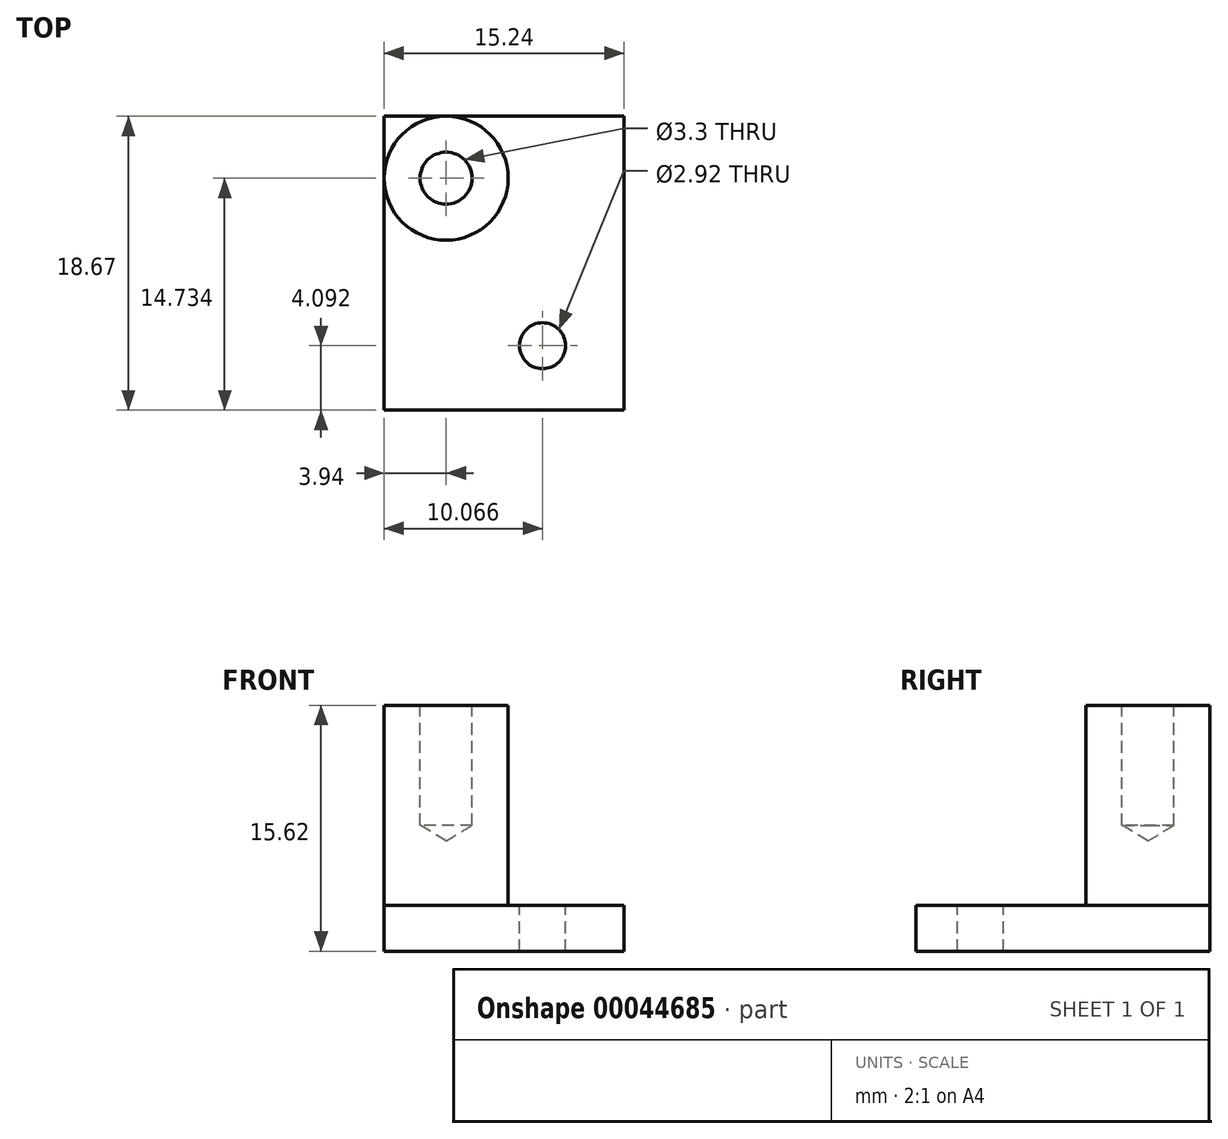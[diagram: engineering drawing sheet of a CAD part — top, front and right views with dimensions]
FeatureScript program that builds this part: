
annotation { "Feature Type Name" : "Feature", "Feature Type Description" : "" }
export const myFeature = defineFeature(function(context is Context, id is Id, definition is map)
    precondition{}
    {
        {
            var Q0;
            Q0=qCreatedBy(makeId("Top.planeOp"),FACE);
            var sketch = newSketch(context, id + "F0", { "sketchPlane" : qUnion([Q0])});
            skLineSegment(sketch, "E0", {"start": v(-28.43, 43.25) * mm, "end": v(-28.43, 24.58) * mm});
            skLineSegment(sketch, "E1", {"start": v(-28.43, 24.58) * mm, "end": v(-13.19, 24.58) * mm});
            skLineSegment(sketch, "E2", {"start": v(-13.19, 24.58) * mm, "end": v(-13.19, 43.25) * mm});
            skLineSegment(sketch, "E3", {"start": v(-13.19, 43.25) * mm, "end": v(-28.43, 43.25) * mm});
            skSolve(sketch);
        }
        {
            var Q0;
            Q0=makeQuery(id+"F0.imprint","IMPRINT",FACE,{"disambiguationData":[TD([[makeQuery(id+"F0.imprint","IMPRINT",EDGE,{"derivedFrom":sQuery(id+"F0.wireOp",EDGE,"E0")}),1.0]])]});
            extrude(context, id + "F1", {"entities" : qUnion([Q0]), "depth" : 2.92 * mm});
        }
        {
            var Q0;
            Q0=makeQuery(id+"F1.opExtrude","CAP_FACE",FACE,{"disambiguationData":[OSD([sQuery(id+"F0.wireOp",EDGE,"E0"),sQuery(id+"F0.wireOp",EDGE,"E1"),sQuery(id+"F0.wireOp",EDGE,"E2"),sQuery(id+"F0.wireOp",EDGE,"E3")])],"isStart":false});
            var sketch = newSketch(context, id + "F2", { "sketchPlane" : qUnion([Q0])});
            skCircle(sketch, "E4", {"center": v(-24.49, 39.31) * mm, "radius": 3.94 * mm});
            skSolve(sketch);
        }
        {
            var Q0;
            {var subQ0=sQuery(id+"F2.wireOp",EDGE,"E4");var subQ1=makeQuery(id+"F2.imprint","INTERSECT",VERTEX,{"derivedFrom":[makeQuery(id+"F1.opExtrude","CAP_EDGE",EDGE,{"disambiguationData":[OSD([sQuery(id+"F0.wireOp",EDGE,"E0")])],"isStart":false}),subQ0]});Q0=makeQuery(id+"F2.imprint","IMPRINT",FACE,{"disambiguationData":[TD([[makeQuery(id+"F2.imprint","IMPRINT",EDGE,{"disambiguationData":[TD([[subQ1,1.0]])],"derivedFrom":subQ0}),1.0]])]});}
            extrude(context, id + "F3", {"entities" : qUnion([Q0]), "operationType" : NewBodyOperationType.ADD, "depth" : 12.7 * mm});
        }
        {
            var Q0;
            Q0=makeQuery(id+"F3.opExtrude","CAP_FACE",FACE,{"disambiguationData":[OSD([sQuery(id+"F2.wireOp",EDGE,"E4")])],"isStart":false});
            var sketch = newSketch(context, id + "F4", { "sketchPlane" : qUnion([Q0])});
            skPoint(sketch, "E5", {"position": v(-24.49, 39.31) * mm});
            skSolve(sketch);
        }
        {
            var Q0;
            Q0=sQuery(id+"F4.wireOp",VERTEX,"E5");
            var Q1;
            Q1=makeQuery(id+"F1.opExtrude","SWEPT_BODY",BODY,{"disambiguationData":[OSD([sQuery(id+"F0.wireOp",EDGE,"E0"),sQuery(id+"F0.wireOp",EDGE,"E1"),sQuery(id+"F0.wireOp",EDGE,"E2"),sQuery(id+"F0.wireOp",EDGE,"E3")])]});
            hole(context, id + "F5", {"style" : HoleStyle.SIMPLE, "holeDiameter" : 3.3 * mm, "endStyle" : HoleEndStyle.BLIND, "holeDepth" : 7.62 * mm, "locations" : qUnion([Q0]), "scope" : qUnion([Q1])});
        }
        {
            var Q0;
            {var subQ0=sQuery(id+"F0.wireOp",EDGE,"E2");var subQ1=sQuery(id+"F0.wireOp",EDGE,"E1");var subQ2=sQuery(id+"F0.wireOp",EDGE,"E3");var subQ3=sQuery(id+"F0.wireOp",EDGE,"E0");var subQ4=makeQuery(id+"F1.opExtrude","CAP_FACE",FACE,{"disambiguationData":[OSD([subQ3,subQ1,subQ0,subQ2])],"isStart":false});Q0=makeQuery(id+"F3.boolean.opBoolean","SPLIT",FACE,{"disambiguationData":[TD([makeQuery(id+"F1.opExtrude","SWEPT_FACE",FACE,{"disambiguationData":[OSD([subQ3])]}),subQ4,makeQuery(id+"F1.opExtrude","SWEPT_FACE",FACE,{"disambiguationData":[OSD([subQ1])]}),makeQuery(id+"F1.opExtrude","SWEPT_FACE",FACE,{"disambiguationData":[OSD([subQ0])]}),makeQuery(id+"F1.opExtrude","SWEPT_FACE",FACE,{"disambiguationData":[OSD([subQ2])]}),makeQuery(id+"F3.opExtrude","SWEPT_FACE",FACE,{"disambiguationData":[OSD([sQuery(id+"F2.wireOp",EDGE,"E4")])]})])],"derivedFrom":subQ4});}
            var sketch = newSketch(context, id + "F6", { "sketchPlane" : qUnion([Q0])});
            skPoint(sketch, "E6", {"position": v(-18.36, 28.67) * mm});
            skSolve(sketch);
        }
        {
            var Q0;
            Q0=sQuery(id+"F6.wireOp",VERTEX,"E6");
            var Q1;
            Q1=makeQuery(id+"F1.opExtrude","SWEPT_BODY",BODY,{"disambiguationData":[OSD([sQuery(id+"F0.wireOp",EDGE,"E0"),sQuery(id+"F0.wireOp",EDGE,"E1"),sQuery(id+"F0.wireOp",EDGE,"E2"),sQuery(id+"F0.wireOp",EDGE,"E3")])]});
            hole(context, id + "F7", {"style" : HoleStyle.SIMPLE, "holeDiameter" : 2.92 * mm, "endStyle" : HoleEndStyle.THROUGH, "locations" : qUnion([Q0]), "scope" : qUnion([Q1])});
        }
    });
